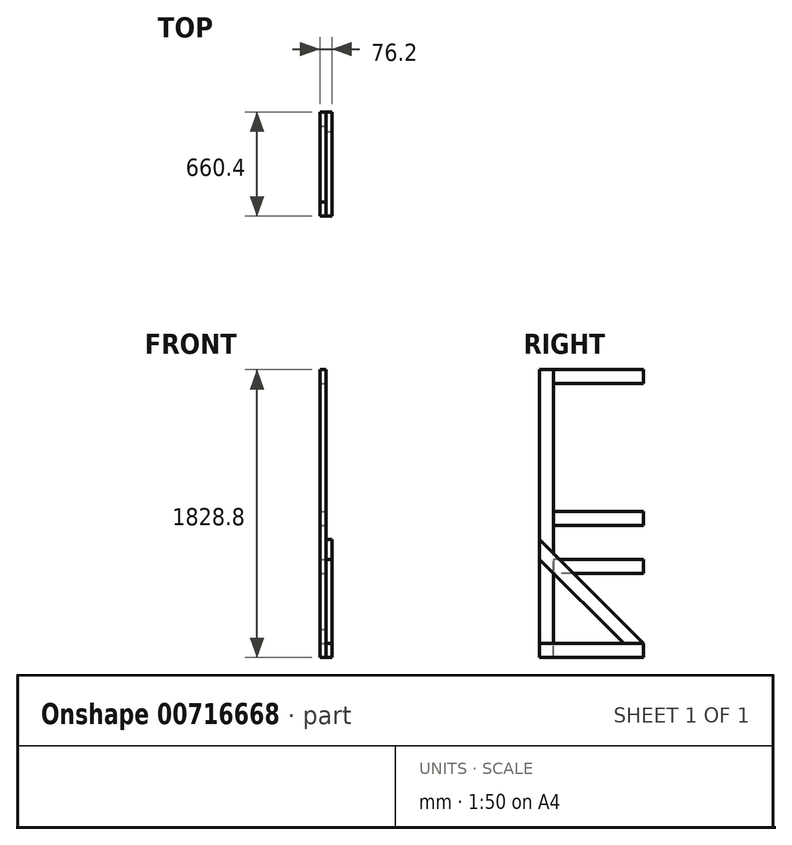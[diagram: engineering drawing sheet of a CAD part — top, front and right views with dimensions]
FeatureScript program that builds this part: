
annotation { "Feature Type Name" : "Feature", "Feature Type Description" : "" }
export const myFeature = defineFeature(function(context is Context, id is Id, definition is map)
    precondition{}
    {
        {
            var Q0;
            Q0=qCreatedBy(makeId("Right.planeOp"),FACE);
            var sketch = newSketch(context, id + "F0", { "sketchPlane" : qUnion([Q0])});
            skLineSegment(sketch, "E0.bottom", {"start": v(0, 0) * mm, "end": v(660.4, 0) * mm});
            skLineSegment(sketch, "E0.top", {"start": v(0, 88.9) * mm, "end": v(660.4, 88.9) * mm});
            skLineSegment(sketch, "E0.left", {"start": v(0, 0) * mm, "end": v(0, 88.9) * mm});
            skLineSegment(sketch, "E0.right", {"start": v(660.4, 0) * mm, "end": v(660.4, 88.9) * mm});
            skSolve(sketch);
        }
        {
            var Q0;
            Q0=makeQuery(id+"F0.imprint","IMPRINT",FACE,{"disambiguationData":[TD([[makeQuery(id+"F0.imprint","IMPRINT",EDGE,{"derivedFrom":sQuery(id+"F0.wireOp",EDGE,"E0.bottom")}),1.0]])]});
            var Q1;
            Q1 = qSketchRegion(id + "F0", true);
            extrude(context, id + "F1", {"entities" : qUnion([Q0, Q1]), "depth" : 38.1 * mm, "offsetDistance" : 25.4 * mm});
        }
        {
            var Q0;
            Q0=qCreatedBy(makeId("Right.planeOp"),FACE);
            var sketch = newSketch(context, id + "F2", { "sketchPlane" : qUnion([Q0])});
            skLineSegment(sketch, "E1.bottom", {"start": v(0, 0) * mm, "end": v(88.9, 0) * mm});
            skLineSegment(sketch, "E1.top", {"start": v(0, 1828.8) * mm, "end": v(88.9, 1828.8) * mm});
            skLineSegment(sketch, "E1.left", {"start": v(0, 0) * mm, "end": v(0, 1828.8) * mm});
            skLineSegment(sketch, "E1.right", {"start": v(88.9, 0) * mm, "end": v(88.9, 1828.8) * mm});
            skSolve(sketch);
        }
        {
            var Q0;
            Q0=makeQuery(id+"F2.imprint","IMPRINT",FACE,{"disambiguationData":[TD([[makeQuery(id+"F2.imprint","IMPRINT",EDGE,{"derivedFrom":sQuery(id+"F2.wireOp",EDGE,"E1.bottom")}),1.0]])]});
            extrude(context, id + "F3", {"entities" : qUnion([Q0]), "oppositeDirection" : true, "depth" : 38.1 * mm, "offsetDistance" : 25.4 * mm});
        }
        {
            var Q0;
            Q0=qCreatedBy(makeId("Right.planeOp"),FACE);
            var sketch = newSketch(context, id + "F4", { "sketchPlane" : qUnion([Q0])});
            skLineSegment(sketch, "E2", {"start": v(0, 749.3) * mm, "end": v(660.4, 88.9) * mm});
            skLineSegment(sketch, "E3", {"start": v(660.4, 88.9) * mm, "end": v(534.68, 88.9) * mm});
            skLineSegment(sketch, "E4", {"start": v(534.68, 88.9) * mm, "end": v(0, 623.58) * mm});
            skLineSegment(sketch, "E5", {"start": v(0, 623.58) * mm, "end": v(0, 749.3) * mm});
            skSolve(sketch);
        }
        {
            var Q0;
            Q0=makeQuery(id+"F4.imprint","IMPRINT",FACE,{"disambiguationData":[TD([[makeQuery(id+"F4.imprint","IMPRINT",EDGE,{"derivedFrom":sQuery(id+"F4.wireOp",EDGE,"E2")}),-1.0]])]});
            extrude(context, id + "F5", {"entities" : qUnion([Q0]), "depth" : 38.1 * mm, "offsetDistance" : 25.4 * mm});
        }
        {
            var Q0;
            Q0=makeQuery(id+"F1.opExtrude","CAP_FACE",FACE,{"disambiguationData":[OSD([sQuery(id+"F0.wireOp",EDGE,"E0.bottom"),sQuery(id+"F0.wireOp",EDGE,"E0.top"),sQuery(id+"F0.wireOp",EDGE,"E0.left"),sQuery(id+"F0.wireOp",EDGE,"E0.right")])],"isStart":true});
            var sketch = newSketch(context, id + "F6", { "sketchPlane" : qUnion([Q0])});
            skLineSegment(sketch, "E6", {"start": v(-660.4, 0) * mm, "end": v(-660.4, 88.9) * mm});
            skLineSegment(sketch, "E7", {"start": v(-660.4, 88.9) * mm, "end": v(-571.5, 177.8) * mm});
            skLineSegment(sketch, "E8", {"start": v(-571.5, 177.8) * mm, "end": v(-571.5, 0) * mm});
            skLineSegment(sketch, "E9", {"start": v(-571.5, 0) * mm, "end": v(-660.4, 0) * mm});
            skSolve(sketch);
        }
        {
            var Q0;
            Q0 = qSketchRegion(id + "F6", true);
            extrude(context, id + "F7", {"entities" : qUnion([Q0]), "depth" : 38.1 * mm, "offsetDistance" : 25.4 * mm});
        }
        {
            var Q0;
            Q0=makeQuery(id+"F5.opExtrude","CAP_FACE",FACE,{"disambiguationData":[OSD([sQuery(id+"F4.wireOp",EDGE,"E2"),sQuery(id+"F4.wireOp",EDGE,"E3"),sQuery(id+"F4.wireOp",EDGE,"E4"),sQuery(id+"F4.wireOp",EDGE,"E5")])],"isStart":true});
            var sketch = newSketch(context, id + "F8", { "sketchPlane" : qUnion([Q0])});
            skLineSegment(sketch, "E10.bottom", {"start": v(-660.4, 623.58) * mm, "end": v(-88.9, 623.58) * mm});
            skLineSegment(sketch, "E10.top", {"start": v(-660.4, 534.68) * mm, "end": v(-88.9, 534.68) * mm});
            skLineSegment(sketch, "E10.left", {"start": v(-660.4, 623.58) * mm, "end": v(-660.4, 534.68) * mm});
            skLineSegment(sketch, "E10.right", {"start": v(-88.9, 623.58) * mm, "end": v(-88.9, 534.68) * mm});
            skSolve(sketch);
        }
        {
            var Q0;
            Q0 = qSketchRegion(id + "F8", true);
            extrude(context, id + "F9", {"entities" : qUnion([Q0]), "depth" : 38.1 * mm, "offsetDistance" : 25.4 * mm});
        }
        {
            var Q0;
            Q0=makeQuery(id+"F9.opExtrude","SWEPT_BODY",BODY,{"disambiguationData":[OSD([sQuery(id+"F8.wireOp",EDGE,"E10.bottom"),sQuery(id+"F8.wireOp",EDGE,"E10.top"),sQuery(id+"F8.wireOp",EDGE,"E10.left"),sQuery(id+"F8.wireOp",EDGE,"E10.right")])]});
            transform(context, id + "F10", {"entities" : qUnion([Q0]), "transformType" : TransformType.TRANSLATION_3D, "dx" : 0 * mm, "dy" : 0 * mm, "dz" : 304.8 * mm, "makeCopy" : true});
        }
        {
            var Q0;
            Q0=makeQuery(id+"F9.opExtrude","SWEPT_EDGE",EDGE,{"disambiguationData":[OSD([sQuery(id+"F8.wireOp",EDGE,"E10.bottom"),sQuery(id+"F8.wireOp",EDGE,"E10.right")])]});
            cPoint(context, id + "F11", {"entities" : qUnion([Q0]), "parameter" : 0.5});
        }
        {
            var Q0;
            Q0=makeQuery(id+"F3.opExtrude","SWEPT_EDGE",EDGE,{"disambiguationData":[OSD([sQuery(id+"F2.wireOp",EDGE,"E1.top"),sQuery(id+"F2.wireOp",EDGE,"E1.right")])]});
            cPoint(context, id + "F12", {"entities" : qUnion([Q0]), "parameter" : 0.5});
        }
        {
            var Q0;
            Q0=makeQuery(id+"F9.opExtrude","SWEPT_BODY",BODY,{"disambiguationData":[OSD([sQuery(id+"F8.wireOp",EDGE,"E10.bottom"),sQuery(id+"F8.wireOp",EDGE,"E10.top"),sQuery(id+"F8.wireOp",EDGE,"E10.left"),sQuery(id+"F8.wireOp",EDGE,"E10.right")])]});
            var Q1;
            Q1 = qCreatedBy(id + "F11" ,VERTEX);
            var Q2;
            Q2 = qCreatedBy(id + "F12" ,VERTEX);
            transform(context, id + "F13", {"entities" : qUnion([Q0]), "transformType" : TransformType.TRANSLATION_ENTITY, "oppositeDirectionEntity" : false, "transformLine" : qUnion([Q1, Q2]), "makeCopy" : true});
        }
    });
